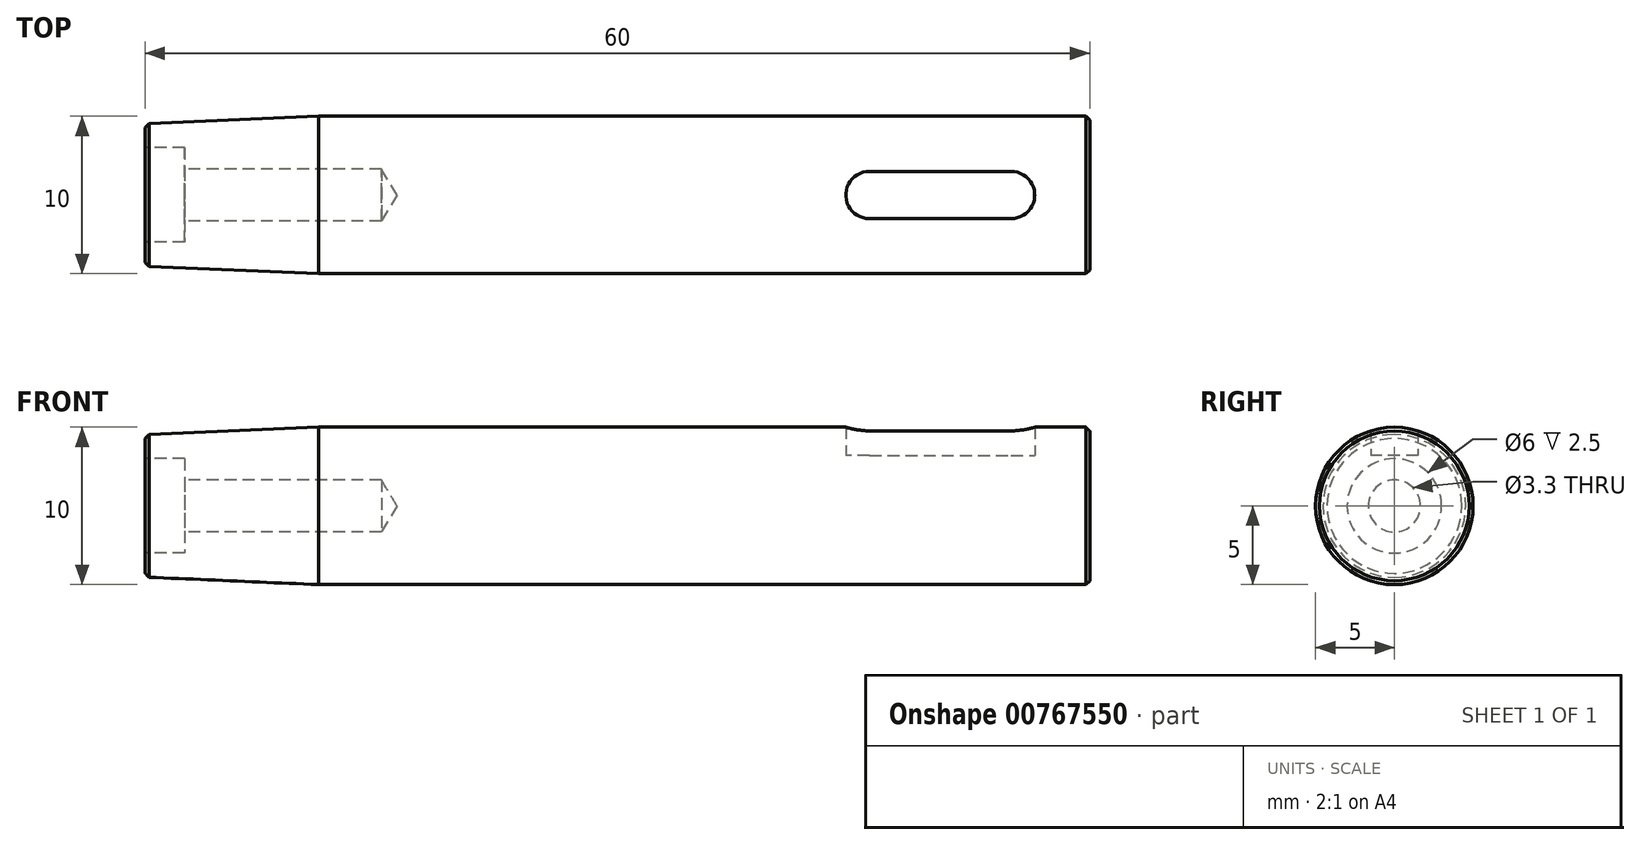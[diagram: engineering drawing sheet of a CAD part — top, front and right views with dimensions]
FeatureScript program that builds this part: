
annotation { "Feature Type Name" : "Feature", "Feature Type Description" : "" }
export const myFeature = defineFeature(function(context is Context, id is Id, definition is map)
    precondition{}
    {
        {
            var Q0;
            Q0=qCreatedBy(makeId("Front.planeOp"),FACE);
            var sketch = newSketch(context, id + "F0", { "sketchPlane" : qUnion([Q0])});
            skLineSegment(sketch, "E0", {"start": v(0, 0) * mm, "end": v(0, 4.52) * mm});
            skLineSegment(sketch, "E1", {"start": v(0, 4.52) * mm, "end": v(11, 5) * mm});
            skLineSegment(sketch, "E2", {"start": v(11, 5) * mm, "end": v(60, 5) * mm});
            skLineSegment(sketch, "E3", {"start": v(60, 5) * mm, "end": v(60, 0) * mm});
            skLineSegment(sketch, "E4", {"start": v(60, 0) * mm, "end": v(0, 0) * mm});
            skSolve(sketch);
        }
        {
            var Q0;
            Q0 = qSketchRegion(id + "F0", true);
            var Q1;
            Q1=sQuery(id+"F0.wireOp",EDGE,"E4");
            revolve(context, id + "F1", {"surfaceOperationType" : NewSurfaceOperationType.NEW, "entities" : qUnion([Q0]), "axis" : qUnion([Q1]), "revolveType" : RevolveType.FULL});
        }
        {
            var Q0;
            Q0=makeQuery(id+"F1.opRevolve","SWEPT_EDGE",EDGE,{"disambiguationData":[OSD([sQuery(id+"F0.wireOp",EDGE,"E0"),sQuery(id+"F0.wireOp",EDGE,"E1")])]});
            var Q1;
            Q1=makeQuery(id+"F1.opRevolve","SWEPT_EDGE",EDGE,{"disambiguationData":[OSD([sQuery(id+"F0.wireOp",EDGE,"E2"),sQuery(id+"F0.wireOp",EDGE,"E3")])]});
            chamfer(context, id + "F2", {"entities" : qUnion([Q0, Q1]), "width" : 0.25 * mm, "tangentPropagation" : true});
        }
        {
            var Q0;
            Q0=qCreatedBy(makeId("Top.planeOp"),FACE);
            var sketch = newSketch(context, id + "F3", { "sketchPlane" : qUnion([Q0])});
            skLineSegment(sketch, "E5", {"start": v(46, 0) * mm, "end": v(55, 0) * mm, "construction": true});
            skArc(sketch, "E6.0.startCap", {"start": v(46, -1.5) * mm, "mid": v(44.5, 0) * mm, "end": v(46, 1.5) * mm});
            skArc(sketch, "E6.0.endCap", {"start": v(55, 1.5) * mm, "mid": v(56.5, 0) * mm, "end": v(55, -1.5) * mm});
            skLineSegment(sketch, "E6.0.left", {"start": v(46, 1.5) * mm, "end": v(55, 1.5) * mm});
            skLineSegment(sketch, "E6.0.right", {"start": v(46, -1.5) * mm, "end": v(55, -1.5) * mm});
            skSolve(sketch);
        }
        {
            var Q0;
            Q0 = qSketchRegion(id + "F3", true);
            extrude(context, id + "F4", {"entities" : qUnion([Q0]), "operationType" : NewBodyOperationType.REMOVE, "depth" : 5 * mm, "offsetDistance" : 25 * mm, "hasSecondDirection" : true, "secondDirectionOppositeDirection" : false, "secondDirectionDepth" : 3.2 * mm});
        }
        {
            var Q0;
            Q0=makeQuery(id+"F1.opRevolve","SWEPT_FACE",FACE,{"disambiguationData":[OSD([sQuery(id+"F0.wireOp",EDGE,"E0")])]});
            var sketch = newSketch(context, id + "F5", { "sketchPlane" : qUnion([Q0])});
            skPoint(sketch, "E7", {"position": v(0, 0) * mm});
            skSolve(sketch);
        }
        {
            var Q0;
            Q0=sQuery(id+"F5.wireOp",VERTEX,"E7");
            var Q1;
            Q1=makeQuery(id+"F1.opRevolve","SWEPT_BODY",BODY,{"disambiguationData":[OSD([sQuery(id+"F0.wireOp",EDGE,"E0"),sQuery(id+"F0.wireOp",EDGE,"E1"),sQuery(id+"F0.wireOp",EDGE,"E2"),sQuery(id+"F0.wireOp",EDGE,"E3"),sQuery(id+"F0.wireOp",EDGE,"E4")])]});
            hole(context, id + "F6", {"style" : HoleStyle.SIMPLE, "endStyle" : HoleEndStyle.BLIND, "standardTappedOrClearance" : lookupTablePath({ "standard" : "ISO", "engagement" : "75%", "pitch" : "0.7 mm", "size" : "M4", "type" : "Tapped" }), "standardBlindInLast" : lookupTablePath({ "standard" : "ISO", "engagement" : "75%", "pitch" : "0.7 mm", "size" : "M4", "type" : "Tapped" }), "holeDiameter" : 3.3 * mm, "majorDiameter" : 4 * mm, "showTappedDepth" : true, "holeDepth" : 15 * mm, "tappedDepth" : 12.2 * mm, "tapClearance" : 4, "startFromSketch" : true, "locations" : qUnion([Q0]), "scope" : qUnion([Q1])});
        }
        {
            var Q0;
            Q0=makeQuery(id+"F1.opRevolve","SWEPT_FACE",FACE,{"disambiguationData":[OSD([sQuery(id+"F0.wireOp",EDGE,"E0")])]});
            var sketch = newSketch(context, id + "F7", { "sketchPlane" : qUnion([Q0])});
            skCircle(sketch, "E8", {"center": v(0, 0) * mm, "radius": 3 * mm});
            skSolve(sketch);
        }
        {
            var Q0;
            Q0 = qSketchRegion(id + "F7", true);
            extrude(context, id + "F8", {"entities" : qUnion([Q0]), "operationType" : NewBodyOperationType.REMOVE, "oppositeDirection" : true, "depth" : 2.5 * mm, "offsetDistance" : 25 * mm});
        }
    });
